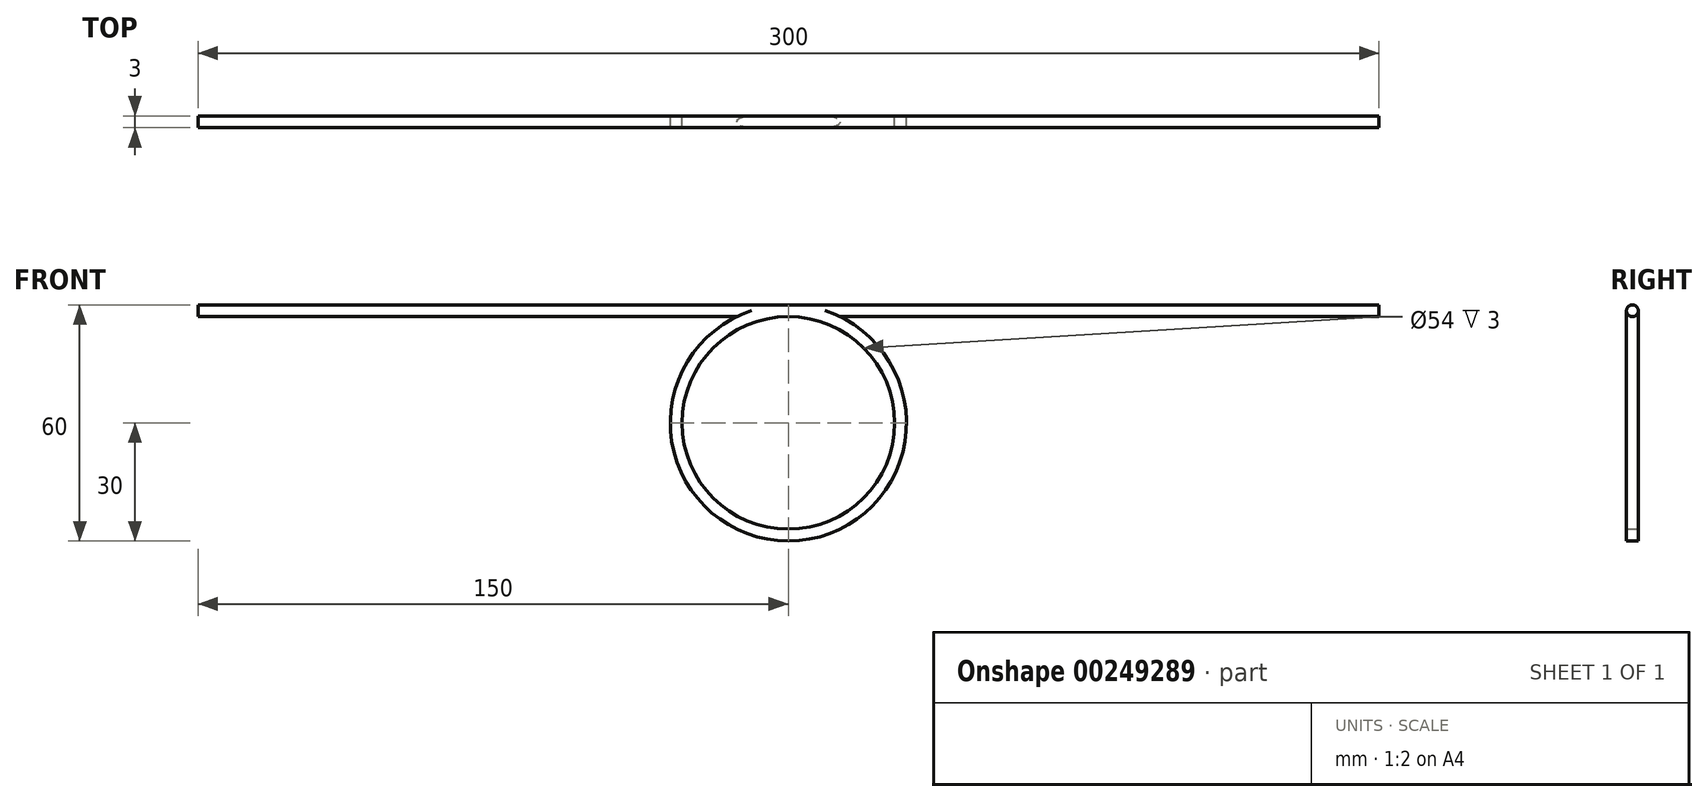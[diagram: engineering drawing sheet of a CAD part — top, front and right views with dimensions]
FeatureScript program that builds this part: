
annotation { "Feature Type Name" : "Feature", "Feature Type Description" : "" }
export const myFeature = defineFeature(function(context is Context, id is Id, definition is map)
    precondition{}
    {
        {
            var Q0;
            Q0=qCreatedBy(makeId("Front.planeOp"),FACE);
            var sketch = newSketch(context, id + "F0", { "sketchPlane" : qUnion([Q0])});
            skLineSegment(sketch, "E0", {"start": v(-150, 0) * mm, "end": v(150, 0) * mm});
            skArc(sketch, "E1", {"start": v(-13.08, -3) * mm, "mid": v(0, -60) * mm, "end": v(13.08, -3) * mm});
            skLineSegment(sketch, "E2", {"start": v(-150, 0) * mm, "end": v(-150, -3) * mm});
            skLineSegment(sketch, "E3", {"start": v(-150, -3) * mm, "end": v(-13.08, -3) * mm});
            skLineSegment(sketch, "E4", {"start": v(150, 0) * mm, "end": v(150, -3) * mm});
            skCircle(sketch, "E5", {"center": v(0, -30) * mm, "radius": 27 * mm});
            skLineSegment(sketch, "E6.trimOffspring", {"start": v(13.08, -3) * mm, "end": v(150, -3) * mm});
            skSolve(sketch);
        }
        {
            var Q0;
            Q0=makeQuery(id+"F0.imprint","IMPRINT",FACE,{"disambiguationData":[TD([[makeQuery(id+"F0.imprint","IMPRINT",EDGE,{"derivedFrom":sQuery(id+"F0.wireOp",EDGE,"E0")}),-1.0]])]});
            extrude(context, id + "F1", {"entities" : qUnion([Q0]), "depth" : 3 * mm, "offsetDistance" : 25 * mm, "symmetric" : true});
        }
        {
            var Q0;
            Q0=makeQuery(id+"F1.opExtrude","CAP_EDGE",EDGE,{"disambiguationData":[OSD([sQuery(id+"F0.wireOp",EDGE,"E3")])],"isStart":false});
            var Q1;
            Q1=makeQuery(id+"F1.opExtrude","CAP_EDGE",EDGE,{"disambiguationData":[OSD([sQuery(id+"F0.wireOp",EDGE,"E0")])],"isStart":false});
            var Q2;
            Q2=makeQuery(id+"F1.opExtrude","CAP_EDGE",EDGE,{"disambiguationData":[OSD([sQuery(id+"F0.wireOp",EDGE,"E0")])],"isStart":true});
            var Q3;
            Q3=makeQuery(id+"F1.opExtrude","CAP_EDGE",EDGE,{"disambiguationData":[OSD([sQuery(id+"F0.wireOp",EDGE,"E3")])],"isStart":true});
            var Q4;
            Q4=makeQuery(id+"F1.opExtrude","CAP_EDGE",EDGE,{"disambiguationData":[OSD([sQuery(id+"F0.wireOp",EDGE,"E6.trimOffspring")])],"isStart":false});
            var Q5;
            Q5=makeQuery(id+"F1.opExtrude","CAP_EDGE",EDGE,{"disambiguationData":[OSD([sQuery(id+"F0.wireOp",EDGE,"E6.trimOffspring")])],"isStart":true});
            fillet(context, id + "F2", {"entities" : qUnion([Q0, Q1, Q2, Q3, Q4, Q5]), "tangentPropagation" : true, "radius" : 1.5 * mm, "defaultsChanged" : false, "vertexSettings" : [], "allowEdgeOverflow" : false});
        }
    });
